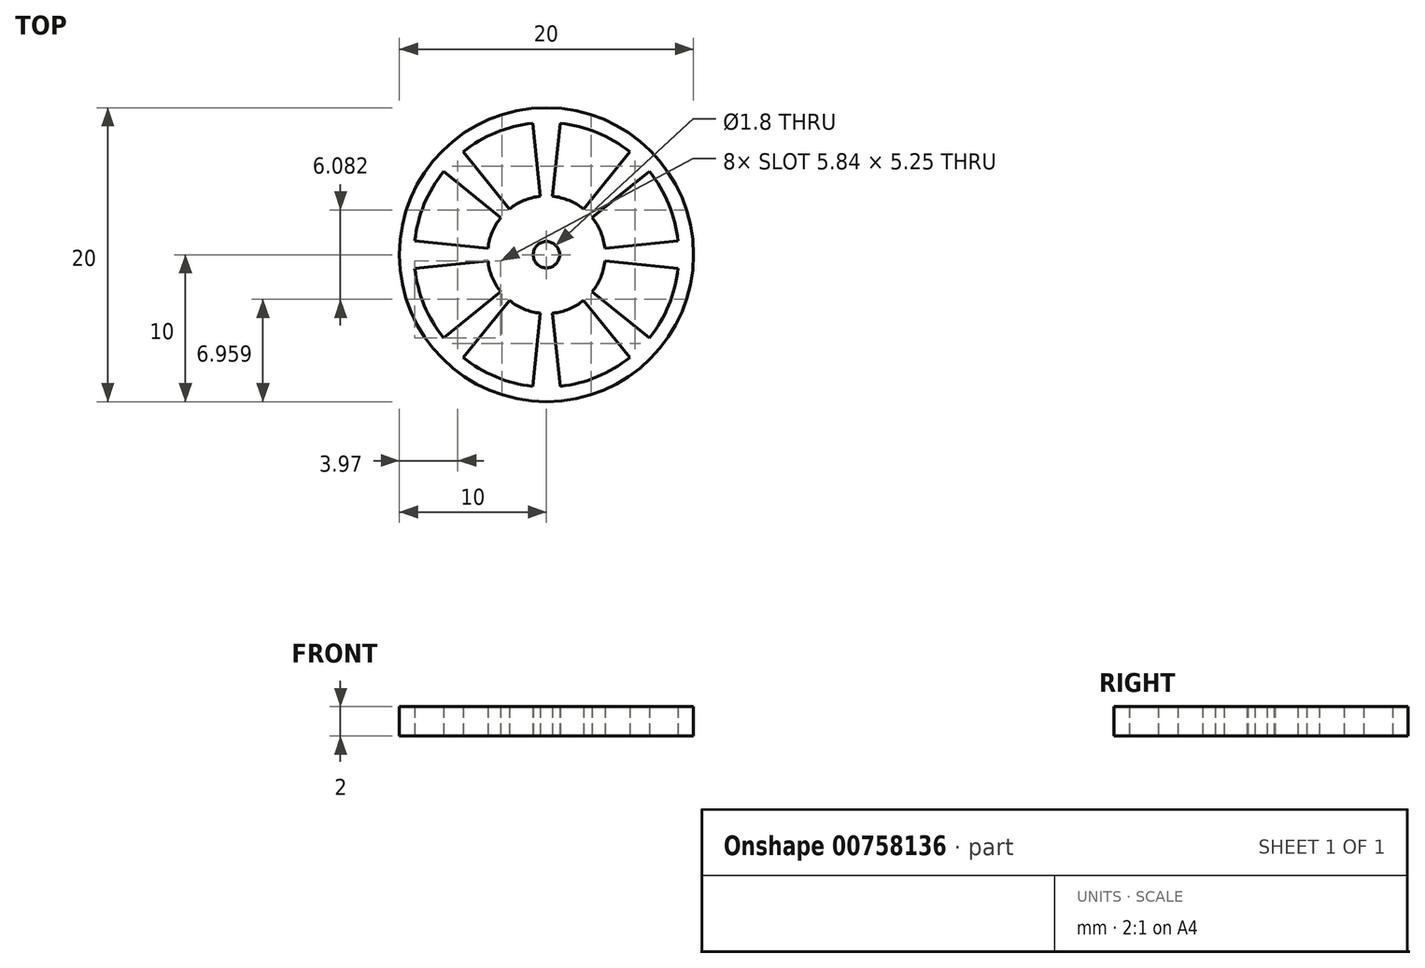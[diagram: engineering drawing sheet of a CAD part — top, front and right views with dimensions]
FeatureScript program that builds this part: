
annotation { "Feature Type Name" : "Feature", "Feature Type Description" : "" }
export const myFeature = defineFeature(function(context is Context, id is Id, definition is map)
    precondition{}
    {
        {
            var Q0;
            Q0=qCreatedBy(makeId("Top.planeOp"),FACE);
            var sketch = newSketch(context, id + "F0", { "sketchPlane" : qUnion([Q0])});
            skCircle(sketch, "E0", {"center": v(0, 0) * mm, "radius": 10 * mm});
            skArc(sketch, "E1", {"start": v(2.52, 3.1) * mm, "mid": v(1.53, 3.7) * mm, "end": v(0.42, 3.98) * mm});
            skArc(sketch, "E2", {"start": v(-8.95, -0.94) * mm, "mid": v(-8.31, -3.44) * mm, "end": v(-7, -5.66) * mm});
            skLineSegment(sketch, "E3.trimOffspring", {"start": v(2.52, 3.1) * mm, "end": v(5.66, 7) * mm});
            skLineSegment(sketch, "E4.trimOffspring", {"start": v(3.1, 2.52) * mm, "end": v(7, 5.66) * mm});
            skLineSegment(sketch, "E5.trimOffspring", {"start": v(0.42, 3.98) * mm, "end": v(0.94, 8.95) * mm});
            skLineSegment(sketch, "E6.trimOffspring", {"start": v(-0.42, 3.98) * mm, "end": v(-0.94, 8.95) * mm});
            skLineSegment(sketch, "E7.trimOffspring", {"start": v(-2.52, 3.1) * mm, "end": v(-5.66, 7) * mm});
            skLineSegment(sketch, "E8.trimOffspring", {"start": v(-3.1, 2.52) * mm, "end": v(-7, 5.66) * mm});
            skLineSegment(sketch, "E9.trimOffspring", {"start": v(3.98, 0.42) * mm, "end": v(8.95, 0.94) * mm});
            skLineSegment(sketch, "E10.trimOffspring", {"start": v(3.1, -2.52) * mm, "end": v(7, -5.66) * mm});
            skLineSegment(sketch, "E11.trimOffspring", {"start": v(2.52, -3.1) * mm, "end": v(5.66, -7) * mm});
            skLineSegment(sketch, "E12.trimOffspring", {"start": v(0.42, -3.98) * mm, "end": v(0.94, -8.95) * mm});
            skLineSegment(sketch, "E13.trimOffspring", {"start": v(-0.42, -3.98) * mm, "end": v(-0.94, -8.95) * mm});
            skLineSegment(sketch, "E14.trimOffspring", {"start": v(-2.52, -3.1) * mm, "end": v(-5.66, -7) * mm});
            skLineSegment(sketch, "E15.trimOffspring", {"start": v(-3.1, -2.52) * mm, "end": v(-7, -5.66) * mm});
            skLineSegment(sketch, "E16.trimOffspring", {"start": v(-3.98, -0.42) * mm, "end": v(-8.95, -0.94) * mm});
            skLineSegment(sketch, "E17.trimOffspring", {"start": v(-3.98, 0.42) * mm, "end": v(-8.95, 0.94) * mm});
            skCircle(sketch, "E18", {"center": v(0, 0) * mm, "radius": 0.9 * mm});
            skLineSegment(sketch, "E19.trimOffspring", {"start": v(3.98, -0.42) * mm, "end": v(8.95, -0.94) * mm});
            skPoint(sketch, "E20.start.orphan", {"position": v(-9, 0) * mm});
            skArc(sketch, "E21.trimOffspring", {"start": v(-7, 5.66) * mm, "mid": v(-8.31, 3.44) * mm, "end": v(-8.95, 0.94) * mm});
            skArc(sketch, "E22.trimOffspring", {"start": v(-0.94, 8.95) * mm, "mid": v(-3.44, 8.31) * mm, "end": v(-5.66, 7) * mm});
            skArc(sketch, "E23.trimOffspring", {"start": v(5.66, 7) * mm, "mid": v(3.44, 8.31) * mm, "end": v(0.94, 8.95) * mm});
            skArc(sketch, "E24.trimOffspring", {"start": v(8.95, 0.94) * mm, "mid": v(8.31, 3.44) * mm, "end": v(7, 5.66) * mm});
            skArc(sketch, "E25.trimOffspring", {"start": v(7, -5.66) * mm, "mid": v(8.31, -3.44) * mm, "end": v(8.95, -0.94) * mm});
            skArc(sketch, "E26.trimOffspring", {"start": v(0.94, -8.95) * mm, "mid": v(3.44, -8.31) * mm, "end": v(5.66, -7) * mm});
            skArc(sketch, "E27.trimOffspring", {"start": v(-5.66, -7) * mm, "mid": v(-3.44, -8.31) * mm, "end": v(-0.94, -8.95) * mm});
            skArc(sketch, "E28.trimOffspring", {"start": v(-0.42, 3.98) * mm, "mid": v(-1.53, 3.7) * mm, "end": v(-2.52, 3.1) * mm});
            skArc(sketch, "E29.trimOffspring", {"start": v(-3.1, 2.52) * mm, "mid": v(-3.7, 1.53) * mm, "end": v(-3.98, 0.42) * mm});
            skArc(sketch, "E30.trimOffspring", {"start": v(-3.98, -0.42) * mm, "mid": v(-3.7, -1.53) * mm, "end": v(-3.1, -2.52) * mm});
            skArc(sketch, "E31.trimOffspring", {"start": v(-2.52, -3.1) * mm, "mid": v(-1.53, -3.7) * mm, "end": v(-0.42, -3.98) * mm});
            skArc(sketch, "E32.trimOffspring", {"start": v(0.42, -3.98) * mm, "mid": v(1.53, -3.7) * mm, "end": v(2.52, -3.1) * mm});
            skArc(sketch, "E33.trimOffspring", {"start": v(3.1, -2.52) * mm, "mid": v(3.7, -1.53) * mm, "end": v(3.98, -0.42) * mm});
            skArc(sketch, "E34.trimOffspring", {"start": v(3.98, 0.42) * mm, "mid": v(3.7, 1.53) * mm, "end": v(3.1, 2.52) * mm});
            skSolve(sketch);
        }
        {
            var Q0;
            Q0=makeQuery(id+"F0.imprint","IMPRINT",FACE,{"disambiguationData":[TD([[makeQuery(id+"F0.imprint","IMPRINT",EDGE,{"derivedFrom":sQuery(id+"F0.wireOp",EDGE,"E0")}),1.0]])]});
            extrude(context, id + "F1", {"entities" : qUnion([Q0]), "depth" : 2 * mm, "offsetDistance" : 25 * mm});
        }
    });
